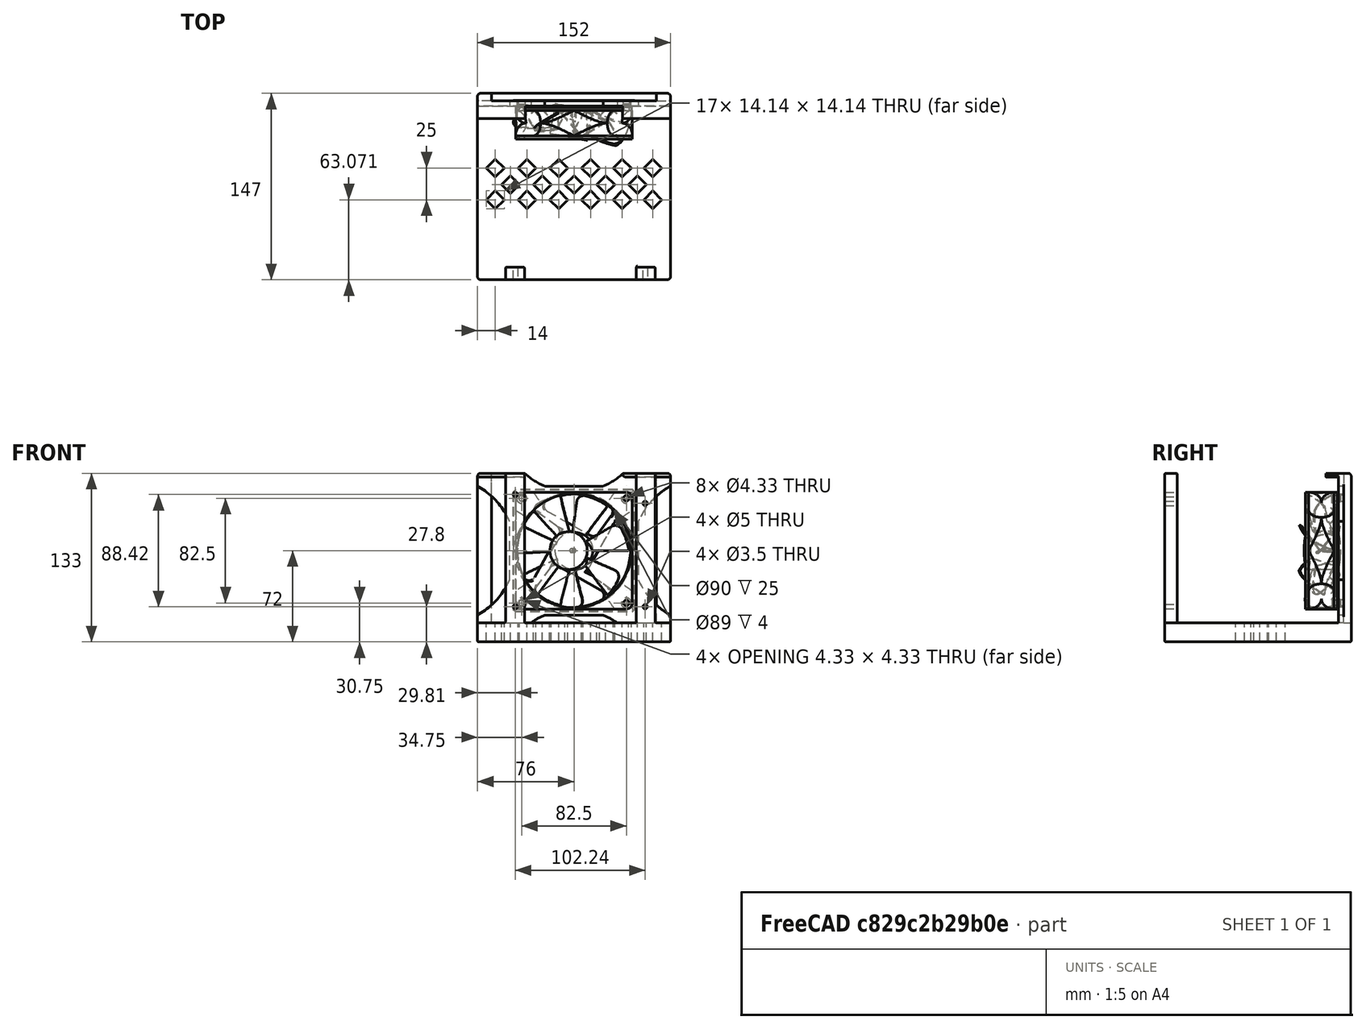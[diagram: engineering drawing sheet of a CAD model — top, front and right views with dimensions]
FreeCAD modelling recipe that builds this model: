
FCSTD DOCUMENT  (FreeCAD 0.21R33668 +7 (Git))
Label: h4MountV2
License: All rights reserved
LicenseURL: http://en.wikipedia.org/wiki/All_rights_reserved
objects: Part::Box×23, Part::MultiFuse×8, Part::Cylinder×4, Part::Feature×3, Part::Fillet×2, Part::Cut×2, Mesh::Feature×1, App::Part×1
note: 42 computed .brp shape members not serialized (recipe doc carries the construction recipe); baked Part::Feature solids carry a one-line shape summary decoded from their .brp

FEATURE [Part::Box] Box  label="Base_Plate"
  AttacherType = Attacher::AttachEngine3D
  Height = 45
  Length = 152
  Placement = pos=(76,6,-57) rot=(0,0.707107,-0.707107;3.14159rad)
  Width = 15
FEATURE [Part::Box] Box001  label="Cube001"
  AttacherType = Attacher::AttachEngine3D
  Height = 118
  Length = 11
  Placement = pos=(65,0,-57) rot=(0,0,1;0rad)
  Width = 6
FEATURE [Part::Box] Box002  label="Cube002"
  AttacherType = Attacher::AttachEngine3D
  Height = 118
  Length = 11
  Placement = pos=(-76,0,-57) rot=(0,0,1;0rad)
  Width = 6
FEATURE [Part::Box] Box004  label="Base_Plate001"
  AttacherType = Attacher::AttachEngine3D
  Height = 102
  Length = 152
  Placement = pos=(76,-39,-57) rot=(0,0.707107,-0.707107;3.14159rad)
  Width = 15
FEATURE [Part::Box] Box005  label="Cube"
  AttacherType = Attacher::AttachEngine3D
  Height = 20
  Length = 10
  Placement = pos=(-60,-60,0) rot=(0,0,1;0.785398rad)
  Width = 10
FEATURE [Part::Box] Box006  label="Cube003"
  AttacherType = Attacher::AttachEngine3D
  Height = 20
  Length = 10
  Placement = pos=(-35,-60,0) rot=(0,0,1;0.785398rad)
  Width = 10
FEATURE [Part::Box] Box007  label="Cube004"
  AttacherType = Attacher::AttachEngine3D
  Height = 20
  Length = 10
  Placement = pos=(-10,-60,0) rot=(0,0,1;0.785398rad)
  Width = 10
FEATURE [Part::Box] Box008  label="Cube005"
  AttacherType = Attacher::AttachEngine3D
  Height = 20
  Length = 10
  Placement = pos=(15,-60,0) rot=(0,0,1;0.785398rad)
  Width = 10
FEATURE [Part::Box] Box009  label="Cube006"
  AttacherType = Attacher::AttachEngine3D
  Height = 20
  Length = 10
  Placement = pos=(40,-60,0) rot=(0,0,1;0.785398rad)
  Width = 10
FEATURE [Part::Box] Box010  label="Cube007"
  AttacherType = Attacher::AttachEngine3D
  Height = 20
  Length = 10
  Placement = pos=(64,-60,0) rot=(0,0,1;0.785398rad)
  Width = 10
FEATURE [Part::Box] Box011  label="Cube008"
  AttacherType = Attacher::AttachEngine3D
  Height = 20
  Length = 10
  Placement = pos=(-60,-60,0) rot=(0,0,1;0.785398rad)
  Width = 10
FEATURE [Part::Box] Box012  label="Cube009"
  AttacherType = Attacher::AttachEngine3D
  Height = 20
  Length = 10
  Placement = pos=(-35,-60,0) rot=(0,0,1;0.785398rad)
  Width = 10
FEATURE [Part::Box] Box013  label="Cube010"
  AttacherType = Attacher::AttachEngine3D
  Height = 20
  Length = 10
  Placement = pos=(-10,-60,0) rot=(0,0,1;0.785398rad)
  Width = 10
FEATURE [Part::Box] Box014  label="Cube011"
  AttacherType = Attacher::AttachEngine3D
  Height = 20
  Length = 10
  Placement = pos=(15,-60,0) rot=(0,0,1;0.785398rad)
  Width = 10
FEATURE [Part::Box] Box015  label="Cube012"
  AttacherType = Attacher::AttachEngine3D
  Height = 20
  Length = 10
  Placement = pos=(40,-60,0) rot=(0,0,1;0.785398rad)
  Width = 10
FEATURE [Part::Box] Box016  label="Cube013"
  AttacherType = Attacher::AttachEngine3D
  Height = 20
  Length = 10
  Placement = pos=(-60,-60,0) rot=(0,0,1;0.785398rad)
  Width = 10
FEATURE [Part::Box] Box017  label="Cube014"
  AttacherType = Attacher::AttachEngine3D
  Height = 20
  Length = 10
  Placement = pos=(-35,-60,0) rot=(0,0,1;0.785398rad)
  Width = 10
FEATURE [Part::Box] Box018  label="Cube015"
  AttacherType = Attacher::AttachEngine3D
  Height = 20
  Length = 10
  Placement = pos=(-10,-60,0) rot=(0,0,1;0.785398rad)
  Width = 10
FEATURE [Part::Box] Box019  label="Cube016"
  AttacherType = Attacher::AttachEngine3D
  Height = 20
  Length = 10
  Placement = pos=(15,-60,0) rot=(0,0,1;0.785398rad)
  Width = 10
FEATURE [Part::Box] Box020  label="Cube017"
  AttacherType = Attacher::AttachEngine3D
  Height = 20
  Length = 10
  Placement = pos=(40,-60,0) rot=(0,0,1;0.785398rad)
  Width = 10
FEATURE [Part::Box] Box021  label="Cube018"
  AttacherType = Attacher::AttachEngine3D
  Height = 20
  Length = 10
  Placement = pos=(64,-60,0) rot=(0,0,1;0.785398rad)
  Width = 10
FEATURE [Part::Box] Box022  label="Cube019"
  AttacherType = Attacher::AttachEngine3D
  Height = 118
  Length = 15
  Placement = pos=(49,-141,-57) rot=(0,0,1;0rad)
  Width = 10
FEATURE [Part::Box] Box023  label="Cube020"
  AttacherType = Attacher::AttachEngine3D
  Height = 118
  Length = 15
  Placement = pos=(-54,-141,-57) rot=(0,0,1;0rad)
  Width = 10
FEATURE [Part::Cylinder] Cylinder
  Angle = 360
  AttacherType = Attacher::AttachEngine3D
  FirstAngle = 0
  Height = 20
  Placement = pos=(-46.19,-136,44.22) rot=(1,0,0;1.5708rad)
  Radius = 1.75
  SecondAngle = 0
FEATURE [Part::Cylinder] Cylinder001
  Angle = 360
  AttacherType = Attacher::AttachEngine3D
  FirstAngle = 0
  Height = 20
  Placement = pos=(-46.19,-136,-44.19) rot=(1,0,0;1.5708rad)
  Radius = 1.75
  SecondAngle = 0
FEATURE [Part::Cylinder] Cylinder002
  Angle = 360
  AttacherType = Attacher::AttachEngine3D
  FirstAngle = 0
  Height = 20
  Placement = pos=(56.05,-136,-44.2) rot=(1,0,0;1.5708rad)
  Radius = 1.75
  SecondAngle = 0
FEATURE [Part::Cylinder] Cylinder003
  Angle = 360
  AttacherType = Attacher::AttachEngine3D
  FirstAngle = 0
  Height = 20
  Placement = pos=(56.05,-136,37.23) rot=(1,0,0;1.5708rad)
  Radius = 1.75
  SecondAngle = 0
FEATURE [Part::MultiFuse] Fusion  label="Base"
  Shapes = -> [Box,Box001,Box002]
FEATURE [Part::Fillet] Fillet  label="Fan_hold"
  Base = -> Fusion
  Edges = 2 edges r=2.5: [Edge7,Edge36]
FEATURE [Part::MultiFuse] Fusion001  label="CubeLine1"
  Placement = pos=(-2,0,0) rot=(0,0,1;0rad)
  Shapes = -> [Box005,Box006,Box007,Box008,Box009,Box010]
FEATURE [Part::MultiFuse] Fusion002  label="CubeLine002"
  Placement = pos=(10,-13,0) rot=(0,0,1;0rad)
  Shapes = -> [Box011,Box012,Box013,Box014,Box015]
FEATURE [Part::MultiFuse] Fusion003  label="CubeLine003"
  Placement = pos=(-2,-25,0) rot=(0,0,1;0rad)
  Shapes = -> [Box016,Box017,Box018,Box019,Box020,Box021]
FEATURE [Part::MultiFuse] Fusion004
  Placement = pos=(0,0,-75) rot=(0,0,1;0rad)
  Shapes = -> [Fusion001,Fusion002,Fusion003]
FEATURE [Part::Cut] Cut  label="BasePlate01"
  Base = -> Box004
  Tool = -> Fusion004
FEATURE [Part::MultiFuse] Fusion005  label="Base_H4"
  Shapes = -> [Cut,Box022,Box023]
FEATURE [Part::MultiFuse] Fusion006  label="Mount_cut"
  Placement = pos=(0,10,0) rot=(0,0,1;0rad)
  Shapes = -> [Cylinder,Cylinder001,Cylinder002,Cylinder003]
FEATURE [Part::Cut] Cut001  label="h4_mount"
  Base = -> Fusion005
  Tool = -> Fusion006
FEATURE [Mesh::Feature] Odroid_H004  label="Odroid-H004"
  Placement = pos=(-50,-110,62) rot=(-1,0,0;1.5708rad)
FEATURE [Part::Feature] Part__Feature  label="fan form"
  Placement = pos=(0,-5,0) rot=(1,0,0;1.5708rad)
  shape: bbox 105.3 x 25.46 x 105.3 mm, 118 faces (baked)
FEATURE [Part::Feature] Part__Feature001  label="fan"
  Placement = pos=(0,-5,0) rot=(0.991837,-0.090167,-0.090167;1.57813rad)
  shape: bbox 92.71 x 38.57 x 91.04 mm, 54 faces (baked)
FEATURE [Part::Feature] Part__Feature002  label="Fan_mount"
  Placement = pos=(0,0,0) rot=(-1,0,0;1.5708rad)
  shape: bbox 152 x 14.25 x 122 mm, 73 faces (baked)
FEATURE [Part::MultiFuse] Fusion007  label="Mount01"
  Shapes = -> [Cut001,Fillet,Part__Feature002]
FEATURE [Part::Fillet] Fillet001  label="Mount"
  Base = -> Fusion007
  Edges = 29 edges: [Edge165 r=2.5,Edge169 r=2.5,Edge171 r=2.5,Edge172 r=1,Edge178 r=1,Edge182 r=1,Edge183 r=1,Edge184 r=1,Edge187 r=1,Edge188 r=1,Edge264 r=1,Edge269 r=2.5,Edge300 r=2.5,Edge301 r=1,Edge302 r=2.5,Edge303 r=1,Edge307 r=1,Edge308 r=1,Edge309 r=1,Edge310 r=1,Edge314 r=1,Edge316 r=1,Edge317 r=1,Edge318 r=1,Edge319 r=1,Edge323 r=1,Edge324 r=1,Edge461 r=1,Edge464 r=1]
FEATURE [App::Part] Assem1  label="h4Mount"
  Group = -> [Part__Feature,Part__Feature001,Fusion003,Fusion006,Fusion007,Fusion,Fusion004,Fusion005,Part__Feature002,Fillet,Fusion001,Fusion002,Box011,Box012,Box013,Box014,Box,Box001,Box002,Box004,Box005,Box006,Box007,Box008,Box009,Box010,Box015,Box016,Box017,Box018,Box019,Box020,Box021,Box022,Box023,Cut,Cut001,Cylinder,Cylinder001,Cylinder002,Cylinder003,Fillet001,Odroid_H004]
  Origin = -> Origin001
  Placement = pos=(46.08,-5.5,0) rot=(1,0,0;1.5708rad)
